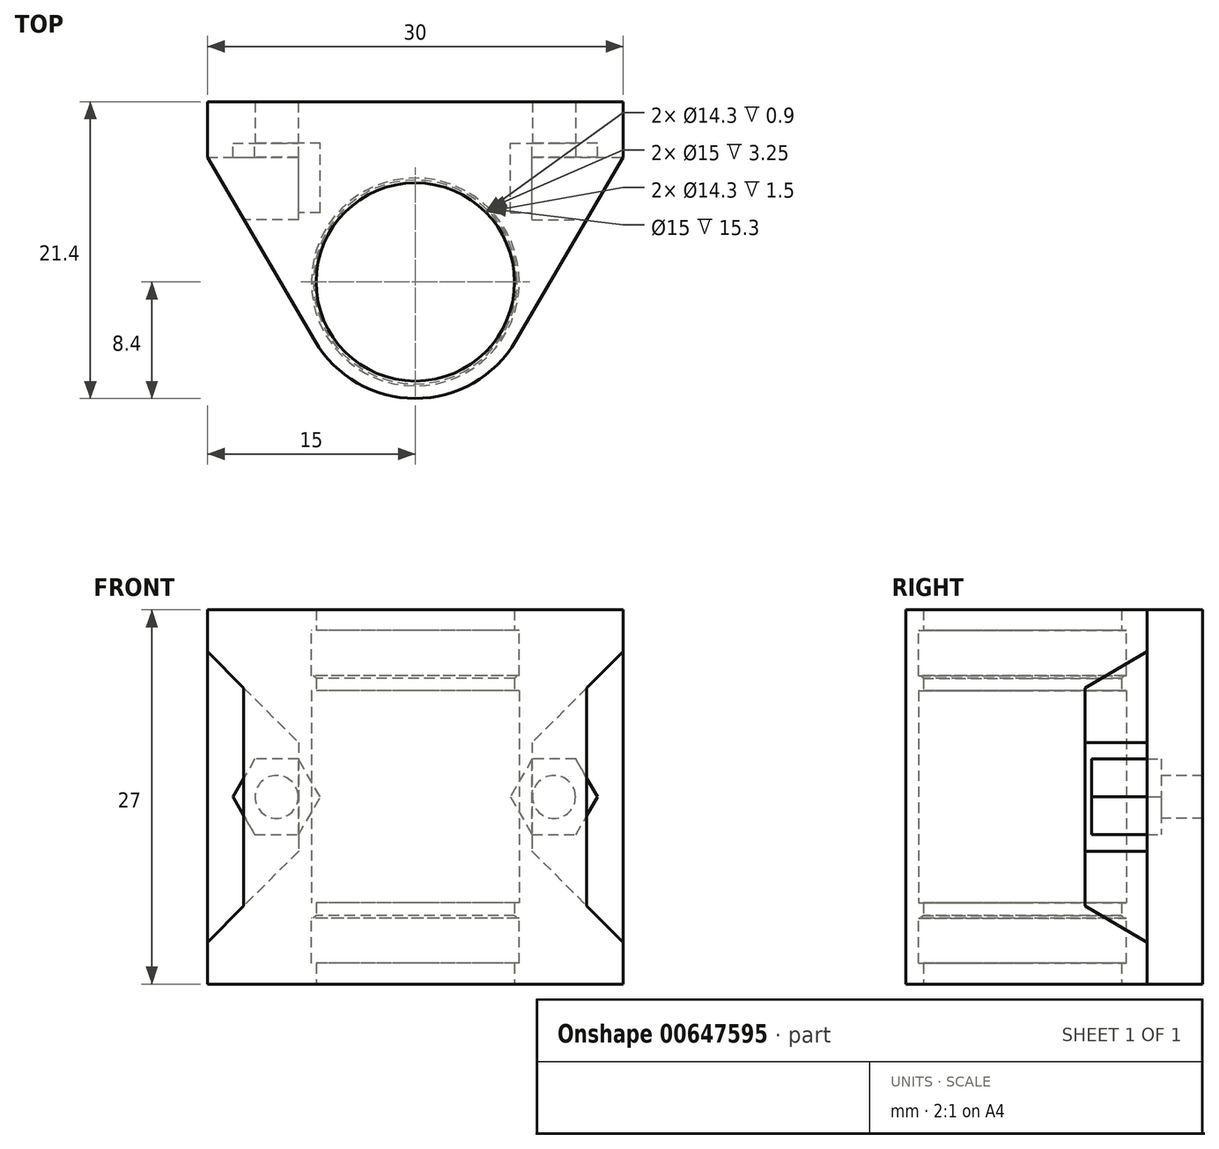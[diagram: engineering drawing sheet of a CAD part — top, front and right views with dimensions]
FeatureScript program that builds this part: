
annotation { "Feature Type Name" : "Feature", "Feature Type Description" : "" }
export const myFeature = defineFeature(function(context is Context, id is Id, definition is map)
    precondition{}
    {
        {
            var Q0;
            Q0=qCreatedBy(makeId("Top.planeOp"),FACE);
            var sketch = newSketch(context, id + "F0", { "sketchPlane" : qUnion([Q0])});
            skCircle(sketch, "E0", {"center": v(0, 0) * mm, "radius": 7.5 * mm});
            skLineSegment(sketch, "E1.top", {"start": v(-15, 9) * mm, "end": v(15, 9) * mm});
            skPoint(sketch, "E2", {"position": v(0, 9) * mm});
            skCircle(sketch, "E3", {"center": v(0, 0) * mm, "radius": 8.4 * mm});
            skCircle(sketch, "E4", {"center": v(0, 0) * mm, "radius": 7.15 * mm});
            skLineSegment(sketch, "E5", {"start": v(-8.27, 1.46) * mm, "end": v(-6.24, 13) * mm});
            skLineSegment(sketch, "E6", {"start": v(8.27, 1.46) * mm, "end": v(6.24, 13) * mm});
            skLineSegment(sketch, "E7", {"start": v(-15, 9) * mm, "end": v(-15, 13) * mm});
            skLineSegment(sketch, "E8", {"start": v(-15, 13) * mm, "end": v(15, 13) * mm});
            skLineSegment(sketch, "E9", {"start": v(15, 13) * mm, "end": v(15, 9) * mm});
            skLineSegment(sketch, "E10", {"start": v(-15, 9) * mm, "end": v(-7.25, -4.24) * mm});
            skLineSegment(sketch, "E11", {"start": v(15, 9) * mm, "end": v(7.25, -4.24) * mm});
            skLineSegment(sketch, "E12", {"start": v(9.73, 0) * mm, "end": v(-9.73, 0) * mm});
            skSolve(sketch);
        }
        {
            var Q0;
            {var subQ0=sQuery(id+"F0.wireOp",EDGE,"E5");var subQ1=sQuery(id+"F0.wireOp",EDGE,"E1.top");var subQ2=makeQuery(id+"F0.imprint","INTERSECT",VERTEX,{"derivedFrom":[subQ1,subQ0]});Q0=makeQuery(id+"F0.imprint","IMPRINT",FACE,{"disambiguationData":[TD([[makeQuery(id+"F0.imprint","IMPRINT",EDGE,{"disambiguationData":[TD([[subQ2,-1.0]])],"derivedFrom":subQ1}),1.0]])]});}
            var Q1;
            {var subQ0=sQuery(id+"F0.wireOp",EDGE,"E5");var subQ1=sQuery(id+"F0.wireOp",EDGE,"E1.top");var subQ2=makeQuery(id+"F0.imprint","INTERSECT",VERTEX,{"derivedFrom":[subQ1,subQ0]});Q1=makeQuery(id+"F0.imprint","IMPRINT",FACE,{"disambiguationData":[TD([[makeQuery(id+"F0.imprint","IMPRINT",EDGE,{"disambiguationData":[TD([[subQ2,-1.0]])],"derivedFrom":subQ1}),-1.0]])]});}
            var Q2;
            {var subQ2=sQuery(id+"F0.wireOp",EDGE,"E12");var subQ6=sQuery(id+"F0.wireOp",EDGE,"E0");var subQ7=makeQuery(id+"F0.imprint","INTERSECT",VERTEX,{"disambiguationData":[OD(0.0)],"derivedFrom":[subQ6,subQ2]});Q2=makeQuery(id+"F0.imprint","IMPRINT",FACE,{"disambiguationData":[TD([[makeQuery(id+"F0.imprint","IMPRINT",EDGE,{"disambiguationData":[TD([[subQ7,-1.0]])],"derivedFrom":subQ6}),-1.0]])]});}
            var Q3;
            {var subQ0=sQuery(id+"F0.wireOp",EDGE,"E12");var subQ1=sQuery(id+"F0.wireOp",EDGE,"E0");var subQ2=makeQuery(id+"F0.imprint","INTERSECT",VERTEX,{"disambiguationData":[OD(0.0)],"derivedFrom":[subQ1,subQ0]});Q3=makeQuery(id+"F0.imprint","IMPRINT",FACE,{"disambiguationData":[TD([[makeQuery(id+"F0.imprint","IMPRINT",EDGE,{"disambiguationData":[TD([[subQ2,-1.0]])],"derivedFrom":subQ1}),1.0]])]});}
            extrude(context, id + "F1", {"entities" : qUnion([Q0, Q1, Q2, Q3]), "depth" : 27 * mm, "offsetDistance" : 25 * mm, "symmetric" : true});
        }
        {
            var Q0;
            {var subQ3=sQuery(id+"F0.wireOp",EDGE,"E5");var subQ5=sQuery(id+"F0.wireOp",EDGE,"2ioF6rcV-CoDT-8IXQ-bcVH-CRvURSwV3O7U");var subQ6=makeQuery(id+"F0.imprint","INTERSECT",VERTEX,{"derivedFrom":[subQ3,subQ5]});Q0=makeQuery(id+"F0.imprint","IMPRINT",FACE,{"disambiguationData":[TD([[makeQuery(id+"F0.imprint","IMPRINT",EDGE,{"disambiguationData":[TD([[subQ6,1.0]])],"derivedFrom":subQ3}),1.0]])]});}
            var Q1;
            {var subQ1=sQuery(id+"F0.wireOp",EDGE,"E1.top");var subQ3=sQuery(id+"F0.wireOp",EDGE,"E5");var subQ4=makeQuery(id+"F0.imprint","INTERSECT",VERTEX,{"derivedFrom":[subQ1,subQ3]});Q1=makeQuery(id+"F0.imprint","IMPRINT",FACE,{"disambiguationData":[TD([[makeQuery(id+"F0.imprint","IMPRINT",EDGE,{"disambiguationData":[TD([[subQ4,1.0]])],"derivedFrom":subQ1}),-1.0]])]});}
            var Q2;
            {var subQ0=sQuery(id+"F0.wireOp",EDGE,"E12");var subQ6=sQuery(id+"F0.wireOp",EDGE,"E0");var subQ8=makeQuery(id+"F0.imprint","INTERSECT",VERTEX,{"disambiguationData":[OD(0.0)],"derivedFrom":[subQ6,subQ0]});Q2=makeQuery(id+"F0.imprint","IMPRINT",FACE,{"disambiguationData":[TD([[makeQuery(id+"F0.imprint","IMPRINT",EDGE,{"disambiguationData":[TD([[subQ8,1.0]])],"derivedFrom":subQ6}),-1.0]])]});}
            var Q3;
            {var subQ1=sQuery(id+"F0.wireOp",EDGE,"E3");var subQ3=sQuery(id+"F0.wireOp",EDGE,"E10");var subQ4=makeQuery(id+"F0.imprint","INTERSECT",VERTEX,{"derivedFrom":[subQ1,subQ3]});Q3=makeQuery(id+"F0.imprint","IMPRINT",FACE,{"disambiguationData":[TD([[makeQuery(id+"F0.imprint","IMPRINT",EDGE,{"disambiguationData":[TD([[subQ4,1.0]])],"derivedFrom":subQ3}),1.0]])]});}
            var Q4;
            {var subQ1=sQuery(id+"F0.wireOp",EDGE,"E3");var subQ3=sQuery(id+"F0.wireOp",EDGE,"E11");var subQ4=makeQuery(id+"F0.imprint","INTERSECT",VERTEX,{"derivedFrom":[subQ1,subQ3]});Q4=makeQuery(id+"F0.imprint","IMPRINT",FACE,{"disambiguationData":[TD([[makeQuery(id+"F0.imprint","IMPRINT",EDGE,{"disambiguationData":[TD([[subQ4,1.0]])],"derivedFrom":subQ3}),-1.0]])]});}
            var Q5;
            {var subQ1=sQuery(id+"F0.wireOp",EDGE,"E1.top");var subQ3=sQuery(id+"F0.wireOp",EDGE,"E6");var subQ4=makeQuery(id+"F0.imprint","INTERSECT",VERTEX,{"derivedFrom":[subQ1,subQ3]});Q5=makeQuery(id+"F0.imprint","IMPRINT",FACE,{"disambiguationData":[TD([[makeQuery(id+"F0.imprint","IMPRINT",EDGE,{"disambiguationData":[TD([[subQ4,-1.0]])],"derivedFrom":subQ1}),-1.0]])]});}
            var Q6;
            {var subQ3=sQuery(id+"F0.wireOp",EDGE,"E6");var subQ5=sQuery(id+"F0.wireOp",EDGE,"2ioF6rcV-CoDT-8IXQ-bcVH-CRvURSwV3O7U");var subQ6=makeQuery(id+"F0.imprint","INTERSECT",VERTEX,{"derivedFrom":[subQ3,subQ5]});Q6=makeQuery(id+"F0.imprint","IMPRINT",FACE,{"disambiguationData":[TD([[makeQuery(id+"F0.imprint","IMPRINT",EDGE,{"disambiguationData":[TD([[subQ6,1.0]])],"derivedFrom":subQ3}),-1.0]])]});}
            var Q7;
            {var subQ0=sQuery(id+"F0.wireOp",EDGE,"E12");var subQ1=sQuery(id+"F0.wireOp",EDGE,"E0");var subQ2=makeQuery(id+"F0.imprint","INTERSECT",VERTEX,{"disambiguationData":[OD(0.0)],"derivedFrom":[subQ1,subQ0]});Q7=makeQuery(id+"F0.imprint","IMPRINT",FACE,{"disambiguationData":[TD([[makeQuery(id+"F0.imprint","IMPRINT",EDGE,{"disambiguationData":[TD([[subQ2,1.0]])],"derivedFrom":subQ1}),1.0]])]});}
            extrude(context, id + "F2", {"entities" : qUnion([Q0, Q1, Q2, Q3, Q4, Q5, Q6, Q7]), "depth" : 27 * mm, "offsetDistance" : 25 * mm, "symmetric" : true});
        }
        {
            var Q0;
            {var subQ0=sQuery(id+"F0.wireOp",EDGE,"E12");var subQ1=sQuery(id+"F0.wireOp",EDGE,"E0");var subQ2=makeQuery(id+"F0.imprint","INTERSECT",VERTEX,{"disambiguationData":[OD(0.0)],"derivedFrom":[subQ1,subQ0]});Q0=makeQuery(id+"F0.imprint","IMPRINT",FACE,{"disambiguationData":[TD([[makeQuery(id+"F0.imprint","IMPRINT",EDGE,{"disambiguationData":[TD([[subQ2,-1.0]])],"derivedFrom":subQ1}),1.0]])]});}
            var Q1;
            {var subQ0=sQuery(id+"F0.wireOp",EDGE,"E12");var subQ1=sQuery(id+"F0.wireOp",EDGE,"E0");var subQ2=makeQuery(id+"F0.imprint","INTERSECT",VERTEX,{"disambiguationData":[OD(0.0)],"derivedFrom":[subQ1,subQ0]});Q1=makeQuery(id+"F0.imprint","IMPRINT",FACE,{"disambiguationData":[TD([[makeQuery(id+"F0.imprint","IMPRINT",EDGE,{"disambiguationData":[TD([[subQ2,1.0]])],"derivedFrom":subQ1}),1.0]])]});}
            extrude(context, id + "F3", {"entities" : qUnion([Q0, Q1]), "operationType" : NewBodyOperationType.REMOVE, "oppositeDirection" : true, "depth" : 24 * mm, "offsetDistance" : 25 * mm, "symmetric" : true});
        }
        {
            var Q0;
            {var subQ0=sQuery(id+"F0.wireOp",EDGE,"E12");var subQ1=sQuery(id+"F0.wireOp",EDGE,"E0");var subQ2=makeQuery(id+"F0.imprint","INTERSECT",VERTEX,{"disambiguationData":[OD(0.0)],"derivedFrom":[subQ1,subQ0]});Q0=makeQuery(id+"F0.imprint","IMPRINT",FACE,{"disambiguationData":[TD([[makeQuery(id+"F0.imprint","IMPRINT",EDGE,{"disambiguationData":[TD([[subQ2,-1.0]])],"derivedFrom":subQ1}),1.0]])]});}
            extrude(context, id + "F4", {"entities" : qUnion([Q0]), "operationType" : NewBodyOperationType.ADD, "depth" : 17.5 * mm, "offsetDistance" : 25 * mm, "symmetric" : true});
        }
        {
            var Q0;
            {var subQ0=sQuery(id+"F0.wireOp",EDGE,"E12");var subQ1=sQuery(id+"F0.wireOp",EDGE,"E0");var subQ2=makeQuery(id+"F0.imprint","INTERSECT",VERTEX,{"disambiguationData":[OD(0.0)],"derivedFrom":[subQ1,subQ0]});Q0=makeQuery(id+"F0.imprint","IMPRINT",FACE,{"disambiguationData":[TD([[makeQuery(id+"F0.imprint","IMPRINT",EDGE,{"disambiguationData":[TD([[subQ2,1.0]])],"derivedFrom":subQ1}),1.0]])]});}
            extrude(context, id + "F5", {"entities" : qUnion([Q0]), "operationType" : NewBodyOperationType.ADD, "depth" : 17.5 * mm, "offsetDistance" : 25 * mm, "symmetric" : true});
        }
        {
            var Q0;
            {var subQ0=sQuery(id+"F0.wireOp",EDGE,"E12");var subQ1=sQuery(id+"F0.wireOp",EDGE,"E0");var subQ2=makeQuery(id+"F0.imprint","INTERSECT",VERTEX,{"disambiguationData":[OD(0.0)],"derivedFrom":[subQ1,subQ0]});Q0=makeQuery(id+"F0.imprint","IMPRINT",FACE,{"disambiguationData":[TD([[makeQuery(id+"F0.imprint","IMPRINT",EDGE,{"disambiguationData":[TD([[subQ2,-1.0]])],"derivedFrom":subQ1}),1.0]])]});}
            var Q1;
            {var subQ0=sQuery(id+"F0.wireOp",EDGE,"E12");var subQ1=sQuery(id+"F0.wireOp",EDGE,"E0");var subQ2=makeQuery(id+"F0.imprint","INTERSECT",VERTEX,{"disambiguationData":[OD(0.0)],"derivedFrom":[subQ1,subQ0]});Q1=makeQuery(id+"F0.imprint","IMPRINT",FACE,{"disambiguationData":[TD([[makeQuery(id+"F0.imprint","IMPRINT",EDGE,{"disambiguationData":[TD([[subQ2,1.0]])],"derivedFrom":subQ1}),1.0]])]});}
            var Q2;
            Q2=makeQuery(id+"F4.opExtrude","CAP_FACE",FACE,{"disambiguationData":[OSD([sQuery(id+"F0.wireOp",EDGE,"E0"),sQuery(id+"F0.wireOp",EDGE,"E4"),sQuery(id+"F0.wireOp",EDGE,"OyqxnQTL-80hJ-Tre8-0LPI-5BT4BykeZ9OB"),sQuery(id+"F0.wireOp",EDGE,"toQEOSAH-RIUy-FKcM-AJDC-1LW4buzCWPbQ")])],"isStart":false});
            var Q3;
            Q3=makeQuery(id+"F4.opExtrude","CAP_FACE",FACE,{"disambiguationData":[OSD([sQuery(id+"F0.wireOp",EDGE,"E0"),sQuery(id+"F0.wireOp",EDGE,"E4"),sQuery(id+"F0.wireOp",EDGE,"OyqxnQTL-80hJ-Tre8-0LPI-5BT4BykeZ9OB"),sQuery(id+"F0.wireOp",EDGE,"toQEOSAH-RIUy-FKcM-AJDC-1LW4buzCWPbQ")])],"isStart":true});
            extrude(context, id + "F6", {"entities" : qUnion([Q0, Q1]), "operationType" : NewBodyOperationType.REMOVE, "endBound" : BoundingType.UP_TO_SURFACE, "depth" : 15 * mm, "endBoundEntityFace" : qUnion([Q2]), "hasOffset" : true, "offsetDistance" : 1.1 * mm, "hasSecondDirection" : true, "secondDirectionBound" : BoundingType.UP_TO_SURFACE, "secondDirectionOppositeDirection" : true, "secondDirectionDepth" : 25 * mm, "secondDirectionBoundEntityFace" : qUnion([Q3]), "hasSecondDirectionOffset" : true, "secondDirectionOffsetDistance" : 1.1 * mm});
        }
        {
            var Q0;
            Q0=makeQuery(id+"F1.opExtrude","SWEPT_FACE",FACE,{"disambiguationData":[OSD([sQuery(id+"F0.wireOp",EDGE,"E8")])]});
            cPlane(context, id + "F7", {"entities" : qUnion([Q0]), "cplaneType" : CPlaneType.OFFSET, "offset" : 4 * mm, "oppositeDirection" : true, "width" : 150 * mm, "height" : 150 * mm});
        }
        {
            var Q0;
            Q0=qCreatedBy(id+"F7.planeOp",FACE);
            var sketch = newSketch(context, id + "F8", { "sketchPlane" : qUnion([Q0])});
            skCircle(sketch, "E13", {"center": v(-10, 0) * mm, "radius": 1.55 * mm});
            skCircle(sketch, "E14", {"center": v(10, 0) * mm, "radius": 1.55 * mm});
            skCircle(sketch, "E15.cCircle", {"center": v(-10, 0) * mm, "radius": 3.15 * mm, "construction": true});
            skLineSegment(sketch, "E15.0", {"start": v(-6.85, 0) * mm, "end": v(-8.43, -2.73) * mm});
            skLineSegment(sketch, "E15.1", {"start": v(-8.43, -2.73) * mm, "end": v(-11.58, -2.73) * mm});
            skLineSegment(sketch, "E15.2", {"start": v(-11.58, -2.73) * mm, "end": v(-13.15, 0) * mm});
            skLineSegment(sketch, "E15.3", {"start": v(-13.15, 0) * mm, "end": v(-11.58, 2.73) * mm});
            skLineSegment(sketch, "E15.4", {"start": v(-11.58, 2.73) * mm, "end": v(-8.43, 2.73) * mm});
            skLineSegment(sketch, "E15.5", {"start": v(-8.43, 2.73) * mm, "end": v(-6.85, 0) * mm});
            skCircle(sketch, "E16.cCircle", {"center": v(10, 0) * mm, "radius": 3.15 * mm, "construction": true});
            skLineSegment(sketch, "E16.0", {"start": v(6.85, 0) * mm, "end": v(8.43, 2.73) * mm});
            skLineSegment(sketch, "E16.1", {"start": v(8.43, 2.73) * mm, "end": v(11.58, 2.73) * mm});
            skLineSegment(sketch, "E16.2", {"start": v(11.58, 2.73) * mm, "end": v(13.15, 0) * mm});
            skLineSegment(sketch, "E16.3", {"start": v(13.15, 0) * mm, "end": v(11.58, -2.73) * mm});
            skLineSegment(sketch, "E16.4", {"start": v(11.58, -2.73) * mm, "end": v(8.43, -2.73) * mm});
            skLineSegment(sketch, "E16.5", {"start": v(8.43, -2.73) * mm, "end": v(6.85, 0) * mm});
            skLineSegment(sketch, "E17", {"start": v(-15, -10.5) * mm, "end": v(-15, 10.5) * mm});
            skLineSegment(sketch, "E18", {"start": v(-15, 10.5) * mm, "end": v(-8.43, 3.92) * mm});
            skLineSegment(sketch, "E19", {"start": v(-8.43, 3.92) * mm, "end": v(-8.43, -3.92) * mm});
            skLineSegment(sketch, "E20", {"start": v(-8.43, -3.92) * mm, "end": v(-15, -10.5) * mm});
            skLineSegment(sketch, "E21", {"start": v(15, 10.5) * mm, "end": v(8.43, 3.92) * mm});
            skLineSegment(sketch, "E22", {"start": v(8.43, 3.92) * mm, "end": v(8.43, -3.92) * mm});
            skLineSegment(sketch, "E23", {"start": v(8.43, -3.92) * mm, "end": v(15, -10.5) * mm});
            skLineSegment(sketch, "E24", {"start": v(15, -10.5) * mm, "end": v(15, 10.5) * mm});
            skPoint(sketch, "E25", {"position": v(-15, 0) * mm});
            skSolve(sketch);
        }
        {
            var Q0;
            {var subQ4=sQuery(id+"F8.wireOp",EDGE,"E15.2");Q0=makeQuery(id+"F8.imprint","IMPRINT",FACE,{"disambiguationData":[TD([[makeQuery(id+"F8.imprint","IMPRINT",EDGE,{"derivedFrom":subQ4}),1.0]])]});}
            var Q1;
            {var subQ5=sQuery(id+"F8.wireOp",EDGE,"E16.2");Q1=makeQuery(id+"F8.imprint","IMPRINT",FACE,{"disambiguationData":[TD([[makeQuery(id+"F8.imprint","IMPRINT",EDGE,{"derivedFrom":subQ5}),1.0]])]});}
            var Q2;
            {var subQ1=sQuery(id+"F8.wireOp",EDGE,"E16.2");Q2=makeQuery(id+"F8.imprint","IMPRINT",FACE,{"disambiguationData":[TD([[makeQuery(id+"F8.imprint","IMPRINT",EDGE,{"derivedFrom":subQ1}),-1.0]])]});}
            var Q3;
            {var subQ0=sQuery(id+"F8.wireOp",EDGE,"E22");var subQ1=sQuery(id+"F8.wireOp",EDGE,"E14");var subQ2=makeQuery(id+"F8.imprint","INTERSECT",VERTEX,{"disambiguationData":[OD(0.0)],"derivedFrom":[subQ1,subQ0]});Q3=makeQuery(id+"F8.imprint","IMPRINT",FACE,{"disambiguationData":[TD([[makeQuery(id+"F8.imprint","IMPRINT",EDGE,{"disambiguationData":[TD([[subQ2,1.0]])],"derivedFrom":subQ1}),1.0]])]});}
            var Q4;
            {var subQ1=sQuery(id+"F8.wireOp",EDGE,"E15.2");Q4=makeQuery(id+"F8.imprint","IMPRINT",FACE,{"disambiguationData":[TD([[makeQuery(id+"F8.imprint","IMPRINT",EDGE,{"derivedFrom":subQ1}),-1.0]])]});}
            var Q5;
            {var subQ0=sQuery(id+"F8.wireOp",EDGE,"E19");var subQ1=sQuery(id+"F8.wireOp",EDGE,"E13");var subQ2=makeQuery(id+"F8.imprint","INTERSECT",VERTEX,{"disambiguationData":[OD(0.0)],"derivedFrom":[subQ1,subQ0]});Q5=makeQuery(id+"F8.imprint","IMPRINT",FACE,{"disambiguationData":[TD([[makeQuery(id+"F8.imprint","IMPRINT",EDGE,{"disambiguationData":[TD([[subQ2,-1.0]])],"derivedFrom":subQ1}),1.0]])]});}
            extrude(context, id + "F9", {"entities" : qUnion([Q0, Q1, Q2, Q3, Q4, Q5]), "operationType" : NewBodyOperationType.REMOVE, "oppositeDirection" : true, "depth" : 4.5 * mm, "offsetDistance" : 25 * mm});
        }
        {
            var Q0;
            {var subQ1=sQuery(id+"F8.wireOp",EDGE,"E15.2");Q0=makeQuery(id+"F8.imprint","IMPRINT",FACE,{"disambiguationData":[TD([[makeQuery(id+"F8.imprint","IMPRINT",EDGE,{"derivedFrom":subQ1}),-1.0]])]});}
            var Q1;
            {var subQ5=sQuery(id+"F8.wireOp",EDGE,"E15.0");Q1=makeQuery(id+"F8.imprint","IMPRINT",FACE,{"disambiguationData":[TD([[makeQuery(id+"F8.imprint","IMPRINT",EDGE,{"derivedFrom":subQ5}),-1.0]])]});}
            var Q2;
            {var subQ0=sQuery(id+"F8.wireOp",EDGE,"E19");var subQ1=sQuery(id+"F8.wireOp",EDGE,"E13");var subQ2=makeQuery(id+"F8.imprint","INTERSECT",VERTEX,{"disambiguationData":[OD(0.0)],"derivedFrom":[subQ1,subQ0]});Q2=makeQuery(id+"F8.imprint","IMPRINT",FACE,{"disambiguationData":[TD([[makeQuery(id+"F8.imprint","IMPRINT",EDGE,{"disambiguationData":[TD([[subQ2,1.0]])],"derivedFrom":subQ1}),1.0]])]});}
            var Q3;
            {var subQ1=sQuery(id+"F8.wireOp",EDGE,"E16.2");Q3=makeQuery(id+"F8.imprint","IMPRINT",FACE,{"disambiguationData":[TD([[makeQuery(id+"F8.imprint","IMPRINT",EDGE,{"derivedFrom":subQ1}),-1.0]])]});}
            var Q4;
            {var subQ0=sQuery(id+"F8.wireOp",EDGE,"E22");var subQ1=sQuery(id+"F8.wireOp",EDGE,"E14");var subQ2=makeQuery(id+"F8.imprint","INTERSECT",VERTEX,{"disambiguationData":[OD(0.0)],"derivedFrom":[subQ1,subQ0]});Q4=makeQuery(id+"F8.imprint","IMPRINT",FACE,{"disambiguationData":[TD([[makeQuery(id+"F8.imprint","IMPRINT",EDGE,{"disambiguationData":[TD([[subQ2,-1.0]])],"derivedFrom":subQ1}),1.0]])]});}
            var Q5;
            {var subQ5=sQuery(id+"F8.wireOp",EDGE,"E16.0");Q5=makeQuery(id+"F8.imprint","IMPRINT",FACE,{"disambiguationData":[TD([[makeQuery(id+"F8.imprint","IMPRINT",EDGE,{"derivedFrom":subQ5}),-1.0]])]});}
            extrude(context, id + "F10", {"entities" : qUnion([Q0, Q1, Q2, Q3, Q4, Q5]), "operationType" : NewBodyOperationType.REMOVE, "oppositeDirection" : true, "depth" : 4 * mm, "offsetDistance" : 25 * mm, "hasSecondDirection" : true, "secondDirectionOppositeDirection" : false, "secondDirectionDepth" : 1 * mm});
        }
        {
            var Q0;
            Q0=makeQuery(id+"F8.imprint","IMPRINT",FACE,{"disambiguationData":[TD([[makeQuery(id+"F8.imprint","IMPRINT",EDGE,{"derivedFrom":sQuery(id+"F8.wireOp",EDGE,"E13")}),1.0]])]});
            var Q1;
            Q1=makeQuery(id+"F8.imprint","IMPRINT",FACE,{"disambiguationData":[TD([[makeQuery(id+"F8.imprint","IMPRINT",EDGE,{"derivedFrom":sQuery(id+"F8.wireOp",EDGE,"E14")}),1.0]])]});
            extrude(context, id + "F11", {"entities" : qUnion([Q0, Q1]), "operationType" : NewBodyOperationType.REMOVE, "endBound" : BoundingType.THROUGH_ALL, "depth" : 25 * mm, "offsetDistance" : 25 * mm});
        }
        {
            var Q0;
            Q0=makeQuery(id+"F4.opExtrude","CAP_EDGE",EDGE,{"disambiguationData":[OSD([sQuery(id+"F0.wireOp",EDGE,"E4")])],"isStart":true});
            var Q1;
            {var subQ0=sQuery(id+"F0.wireOp",EDGE,"E4");var subQ1=sQuery(id+"F0.wireOp",EDGE,"E12");var subQ2=sQuery(id+"F0.wireOp",EDGE,"E0");var subQ3=makeQuery(id+"F0.imprint","INTERSECT",VERTEX,{"disambiguationData":[OD(0.0)],"derivedFrom":[subQ0,subQ1]});Q1=makeQuery(id+"F6.boolean.opBoolean","COPY",EDGE,{"disambiguationData":[topologyDisambiguationEdgeConnected([makeQuery(id+"F4.opExtrude","SWEPT_FACE",FACE,{"disambiguationData":[OSD([subQ0])]})])],"derivedFrom":makeQuery(id+"F6.opExtrude","TWEAK_EDGE",EDGE,{"derivedFrom":[makeQuery(id+"F0.imprint","IMPRINT",EDGE,{"disambiguationData":[TD([[subQ3,-1.0]])],"derivedFrom":subQ0}),makeQuery(id+"F0.imprint","IMPRINT",EDGE,{"disambiguationData":[TD([[subQ3,1.0]])],"derivedFrom":subQ0}),makeQuery(id+"F4.opExtrude","CAP_FACE",FACE,{"disambiguationData":[OSD([subQ2,subQ0,subQ1])],"isStart":true})]})});}
            var Q2;
            {var subQ0=sQuery(id+"F0.wireOp",EDGE,"E4");Q2=makeQuery(id+"F3.boolean.opBoolean","COPY",EDGE,{"disambiguationData":[topologyDisambiguationEdgeConnected([makeQuery(id+"F1.opExtrude","SWEPT_FACE",FACE,{"disambiguationData":[OSD([subQ0])]})])],"derivedFrom":makeQuery(id+"F3.opExtrude","CAP_EDGE",EDGE,{"disambiguationData":[OSD([subQ0])],"isStart":false})});}
            var Q3;
            {var subQ0=sQuery(id+"F0.wireOp",EDGE,"E4");var subQ1=sQuery(id+"F0.wireOp",EDGE,"E12");var subQ2=sQuery(id+"F0.wireOp",EDGE,"E0");var subQ3=makeQuery(id+"F0.imprint","INTERSECT",VERTEX,{"disambiguationData":[OD(0.0)],"derivedFrom":[subQ0,subQ1]});Q3=makeQuery(id+"F6.boolean.opBoolean","COPY",EDGE,{"disambiguationData":[topologyDisambiguationEdgeConnected([makeQuery(id+"F4.opExtrude","SWEPT_FACE",FACE,{"disambiguationData":[OSD([subQ0])]})])],"derivedFrom":makeQuery(id+"F6.opExtrude","TWEAK_EDGE",EDGE,{"derivedFrom":[makeQuery(id+"F0.imprint","IMPRINT",EDGE,{"disambiguationData":[TD([[subQ3,-1.0]])],"derivedFrom":subQ0}),makeQuery(id+"F0.imprint","IMPRINT",EDGE,{"disambiguationData":[TD([[subQ3,1.0]])],"derivedFrom":subQ0}),makeQuery(id+"F4.opExtrude","CAP_FACE",FACE,{"disambiguationData":[OSD([subQ2,subQ0,subQ1])],"isStart":false})]})});}
            var Q4;
            Q4=makeQuery(id+"F4.opExtrude","CAP_EDGE",EDGE,{"disambiguationData":[OSD([sQuery(id+"F0.wireOp",EDGE,"E4")])],"isStart":false});
            var Q5;
            {var subQ0=sQuery(id+"F0.wireOp",EDGE,"E4");Q5=makeQuery(id+"F3.boolean.opBoolean","COPY",EDGE,{"disambiguationData":[topologyDisambiguationEdgeConnected([makeQuery(id+"F1.opExtrude","SWEPT_FACE",FACE,{"disambiguationData":[OSD([subQ0])]})])],"derivedFrom":makeQuery(id+"F3.opExtrude","CAP_EDGE",EDGE,{"disambiguationData":[OSD([subQ0])],"isStart":true})});}
            var Q6;
            {var subQ0=sQuery(id+"F0.wireOp",EDGE,"E4");Q6=makeQuery(id+"F3.boolean.opBoolean","COPY",EDGE,{"disambiguationData":[topologyDisambiguationEdgeConnected([makeQuery(id+"F2.opExtrude","SWEPT_FACE",FACE,{"disambiguationData":[OSD([subQ0])]})])],"derivedFrom":makeQuery(id+"F3.opExtrude","CAP_EDGE",EDGE,{"disambiguationData":[OSD([subQ0])],"isStart":false})});}
            var Q7;
            Q7=makeQuery(id+"F5.opExtrude","CAP_EDGE",EDGE,{"disambiguationData":[OSD([sQuery(id+"F0.wireOp",EDGE,"E4")])],"isStart":true});
            var Q8;
            {var subQ0=sQuery(id+"F0.wireOp",EDGE,"E4");var subQ1=sQuery(id+"F0.wireOp",EDGE,"E12");var subQ2=sQuery(id+"F0.wireOp",EDGE,"E0");var subQ3=makeQuery(id+"F0.imprint","INTERSECT",VERTEX,{"disambiguationData":[OD(0.0)],"derivedFrom":[subQ0,subQ1]});Q8=makeQuery(id+"F6.boolean.opBoolean","COPY",EDGE,{"disambiguationData":[topologyDisambiguationEdgeConnected([makeQuery(id+"F5.opExtrude","SWEPT_FACE",FACE,{"disambiguationData":[OSD([subQ0])]})])],"derivedFrom":makeQuery(id+"F6.opExtrude","TWEAK_EDGE",EDGE,{"derivedFrom":[makeQuery(id+"F0.imprint","IMPRINT",EDGE,{"disambiguationData":[TD([[subQ3,-1.0]])],"derivedFrom":subQ0}),makeQuery(id+"F0.imprint","IMPRINT",EDGE,{"disambiguationData":[TD([[subQ3,1.0]])],"derivedFrom":subQ0}),makeQuery(id+"F4.opExtrude","CAP_FACE",FACE,{"disambiguationData":[OSD([subQ2,subQ0,subQ1])],"isStart":true})]})});}
            var Q9;
            {var subQ0=sQuery(id+"F0.wireOp",EDGE,"E4");var subQ1=sQuery(id+"F0.wireOp",EDGE,"E12");var subQ2=sQuery(id+"F0.wireOp",EDGE,"E0");var subQ3=makeQuery(id+"F0.imprint","INTERSECT",VERTEX,{"disambiguationData":[OD(0.0)],"derivedFrom":[subQ0,subQ1]});Q9=makeQuery(id+"F6.boolean.opBoolean","COPY",EDGE,{"disambiguationData":[topologyDisambiguationEdgeConnected([makeQuery(id+"F5.opExtrude","SWEPT_FACE",FACE,{"disambiguationData":[OSD([subQ0])]})])],"derivedFrom":makeQuery(id+"F6.opExtrude","TWEAK_EDGE",EDGE,{"derivedFrom":[makeQuery(id+"F0.imprint","IMPRINT",EDGE,{"disambiguationData":[TD([[subQ3,-1.0]])],"derivedFrom":subQ0}),makeQuery(id+"F0.imprint","IMPRINT",EDGE,{"disambiguationData":[TD([[subQ3,1.0]])],"derivedFrom":subQ0}),makeQuery(id+"F4.opExtrude","CAP_FACE",FACE,{"disambiguationData":[OSD([subQ2,subQ0,subQ1])],"isStart":false})]})});}
            var Q10;
            Q10=makeQuery(id+"F5.opExtrude","CAP_EDGE",EDGE,{"disambiguationData":[OSD([sQuery(id+"F0.wireOp",EDGE,"E4")])],"isStart":false});
            var Q11;
            {var subQ0=sQuery(id+"F0.wireOp",EDGE,"E4");Q11=makeQuery(id+"F3.boolean.opBoolean","COPY",EDGE,{"disambiguationData":[topologyDisambiguationEdgeConnected([makeQuery(id+"F2.opExtrude","SWEPT_FACE",FACE,{"disambiguationData":[OSD([subQ0])]})])],"derivedFrom":makeQuery(id+"F3.opExtrude","CAP_EDGE",EDGE,{"disambiguationData":[OSD([subQ0])],"isStart":true})});}
            chamfer(context, id + "F12", {"entities" : qUnion([Q0, Q1, Q2, Q3, Q4, Q5, Q6, Q7, Q8, Q9, Q10, Q11]), "width" : .2 * mm, "tangentPropagation" : true});
        }
    });
